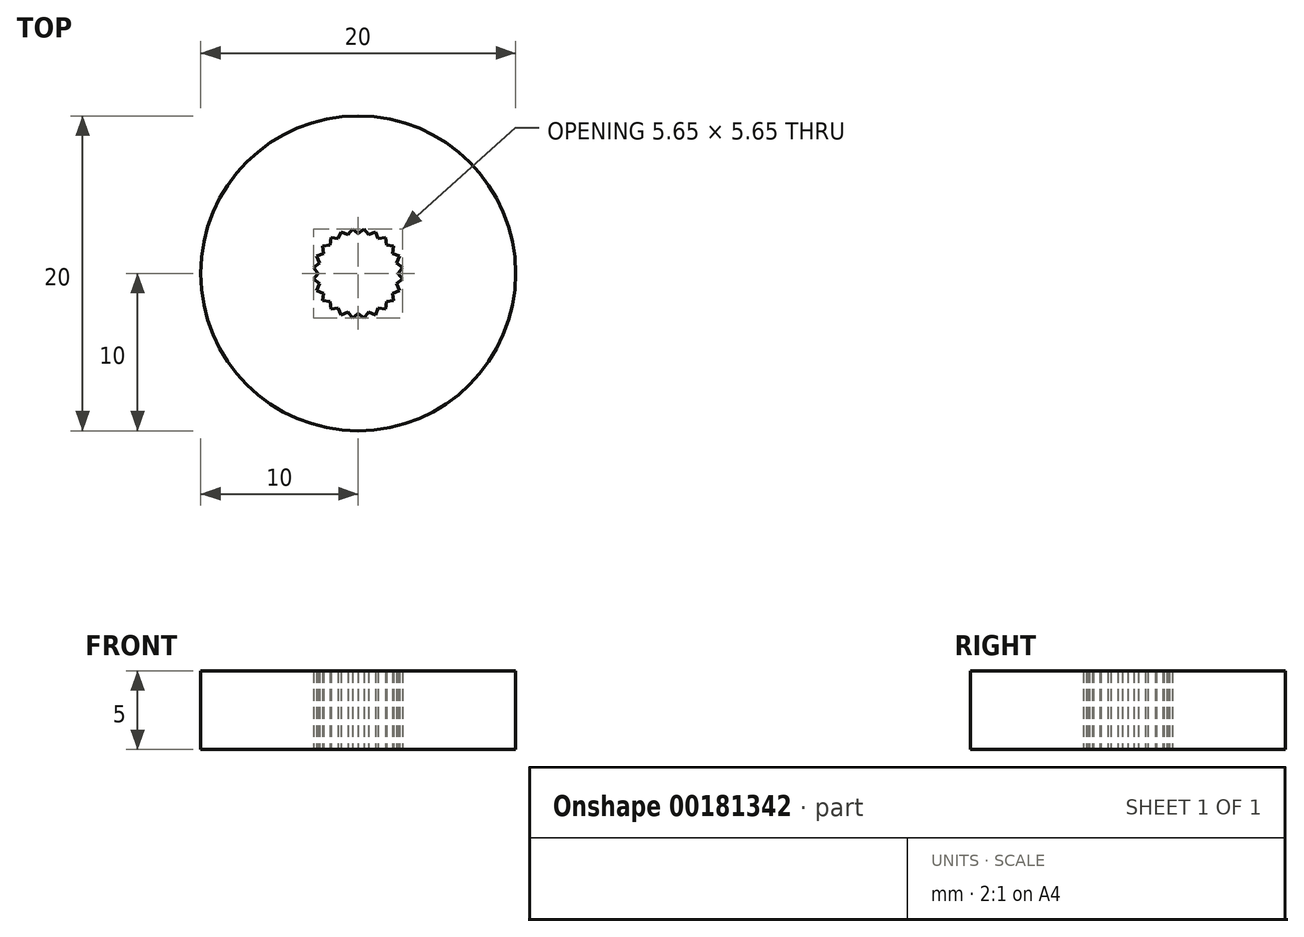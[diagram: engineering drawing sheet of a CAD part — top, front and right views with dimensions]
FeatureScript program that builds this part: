
annotation { "Feature Type Name" : "Feature", "Feature Type Description" : "" }
export const myFeature = defineFeature(function(context is Context, id is Id, definition is map)
    precondition{}
    {
        {
            var Q0;
            Q0=qCreatedBy(makeId("Top.planeOp"),FACE);
            var sketch = newSketch(context, id + "F0", { "sketchPlane" : qUnion([Q0])});
            skPoint(sketch, "E0", {"position": v(0, 2.54) * mm});
            skPoint(sketch, "E1", {"position": v(0.37, 2.83) * mm});
            skLineSegment(sketch, "E2", {"start": v(0, 2.54) * mm, "end": v(0.37, 2.83) * mm});
            skLineSegment(sketch, "E3", {"start": v(0, 2.54) * mm, "end": v(-0.37, 2.83) * mm});
            skLineSegment(sketch, "E4", {"start": v(0.37, 2.83) * mm, "end": v(0.66, 2.45) * mm});
            skLineSegment(sketch, "E5", {"start": v(0.66, 2.45) * mm, "end": v(1.1, 2.63) * mm});
            skLineSegment(sketch, "E6", {"start": v(1.27, 2.2) * mm, "end": v(1.1, 2.63) * mm});
            skLineSegment(sketch, "E7", {"start": v(1.73, 2.26) * mm, "end": v(1.27, 2.2) * mm});
            skLineSegment(sketch, "E8", {"start": v(1.8, 1.8) * mm, "end": v(1.73, 2.26) * mm});
            skLineSegment(sketch, "E9", {"start": v(2.26, 1.73) * mm, "end": v(1.8, 1.8) * mm});
            skLineSegment(sketch, "E10", {"start": v(2.2, 1.27) * mm, "end": v(2.26, 1.73) * mm});
            skLineSegment(sketch, "E11", {"start": v(2.2, 1.27) * mm, "end": v(2.63, 1.1) * mm});
            skLineSegment(sketch, "E12", {"start": v(2.63, 1.1) * mm, "end": v(2.45, 0.66) * mm});
            skLineSegment(sketch, "E13", {"start": v(2.45, 0.66) * mm, "end": v(2.83, 0.37) * mm});
            skLineSegment(sketch, "E14", {"start": v(2.83, 0.37) * mm, "end": v(2.54, 0) * mm});
            skLineSegment(sketch, "E15", {"start": v(2.54, 0) * mm, "end": v(2.83, -0.37) * mm});
            skLineSegment(sketch, "E16", {"start": v(2.83, -0.37) * mm, "end": v(2.45, -0.66) * mm});
            skLineSegment(sketch, "E17", {"start": v(2.45, -0.66) * mm, "end": v(2.63, -1.1) * mm});
            skLineSegment(sketch, "E18", {"start": v(2.63, -1.1) * mm, "end": v(2.2, -1.27) * mm});
            skLineSegment(sketch, "E19", {"start": v(2.2, -1.27) * mm, "end": v(2.26, -1.73) * mm});
            skLineSegment(sketch, "E20", {"start": v(2.26, -1.73) * mm, "end": v(1.8, -1.8) * mm});
            skLineSegment(sketch, "E21", {"start": v(1.8, -1.8) * mm, "end": v(1.73, -2.26) * mm});
            skLineSegment(sketch, "E22", {"start": v(1.73, -2.26) * mm, "end": v(1.27, -2.2) * mm});
            skLineSegment(sketch, "E23", {"start": v(1.27, -2.2) * mm, "end": v(1.1, -2.63) * mm});
            skLineSegment(sketch, "E24", {"start": v(1.1, -2.63) * mm, "end": v(0.66, -2.45) * mm});
            skLineSegment(sketch, "E25", {"start": v(0.66, -2.45) * mm, "end": v(0.37, -2.83) * mm});
            skLineSegment(sketch, "E26", {"start": v(0.37, -2.83) * mm, "end": v(0, -2.54) * mm});
            skLineSegment(sketch, "E27", {"start": v(0, -2.54) * mm, "end": v(-0.37, -2.83) * mm});
            skLineSegment(sketch, "E28", {"start": v(-0.37, -2.83) * mm, "end": v(-0.66, -2.45) * mm});
            skLineSegment(sketch, "E29", {"start": v(-0.66, -2.45) * mm, "end": v(-1.1, -2.63) * mm});
            skLineSegment(sketch, "E30", {"start": v(-1.1, -2.63) * mm, "end": v(-1.27, -2.2) * mm});
            skLineSegment(sketch, "E31", {"start": v(-1.27, -2.2) * mm, "end": v(-1.73, -2.26) * mm});
            skLineSegment(sketch, "E32", {"start": v(-1.73, -2.26) * mm, "end": v(-1.8, -1.8) * mm});
            skLineSegment(sketch, "E33", {"start": v(-1.8, -1.8) * mm, "end": v(-2.26, -1.73) * mm});
            skLineSegment(sketch, "E34", {"start": v(-2.26, -1.73) * mm, "end": v(-2.2, -1.27) * mm});
            skLineSegment(sketch, "E35", {"start": v(-2.63, -1.1) * mm, "end": v(-2.2, -1.27) * mm});
            skLineSegment(sketch, "E36", {"start": v(-2.63, -1.1) * mm, "end": v(-2.45, -0.66) * mm});
            skLineSegment(sketch, "E37", {"start": v(-2.45, -0.66) * mm, "end": v(-2.83, -0.37) * mm});
            skLineSegment(sketch, "E38", {"start": v(-2.83, -0.37) * mm, "end": v(-2.54, 0) * mm});
            skLineSegment(sketch, "E39", {"start": v(-2.54, 0) * mm, "end": v(-2.83, 0.37) * mm});
            skLineSegment(sketch, "E40", {"start": v(-2.83, 0.37) * mm, "end": v(-2.45, 0.66) * mm});
            skLineSegment(sketch, "E41", {"start": v(-2.63, 1.1) * mm, "end": v(-2.45, 0.66) * mm});
            skLineSegment(sketch, "E42", {"start": v(-2.2, 1.27) * mm, "end": v(-2.63, 1.1) * mm});
            skLineSegment(sketch, "E43", {"start": v(-2.26, 1.73) * mm, "end": v(-2.2, 1.27) * mm});
            skLineSegment(sketch, "E44", {"start": v(-2.26, 1.73) * mm, "end": v(-1.8, 1.8) * mm});
            skLineSegment(sketch, "E45", {"start": v(-1.8, 1.8) * mm, "end": v(-1.73, 2.26) * mm});
            skLineSegment(sketch, "E46", {"start": v(-1.73, 2.26) * mm, "end": v(-1.27, 2.2) * mm});
            skLineSegment(sketch, "E47", {"start": v(-1.27, 2.2) * mm, "end": v(-1.1, 2.63) * mm});
            skLineSegment(sketch, "E48", {"start": v(-1.1, 2.63) * mm, "end": v(-0.66, 2.45) * mm});
            skLineSegment(sketch, "E49", {"start": v(-0.66, 2.45) * mm, "end": v(-0.37, 2.83) * mm});
            skCircle(sketch, "E50", {"center": v(0, 0) * mm, "radius": 10 * mm});
            skSolve(sketch);
        }
        {
            var Q0;
            Q0 = qSketchRegion(id + "F0", true);
            extrude(context, id + "F1", {"entities" : qUnion([Q0]), "depth" : 5 * mm});
        }
    });
